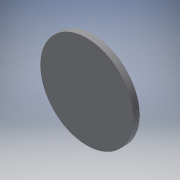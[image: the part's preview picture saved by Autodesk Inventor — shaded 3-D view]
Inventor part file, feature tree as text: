
AUTODESK INVENTOR PART (.ipt)
format: ipt  version: 2016 (Build 200138000, 138)  size: 87,552 bytes
history: native  units: in
note: dims shown in document units (in); Inventor stores cm internally (conversion verified against a paired STEP export)
features: extrude x1, sketch x1, reference x1
ambient origin geometry x8: Origin, YZ Plane, XZ Plane, XY Plane, X Axis, Y Axis, Z Axis, Center Point
bodies: Solid1 (feature_tree)
feature tree (3):
  extrude  "Extrusion1"  Depth=0.0394in TaperAngle=0.0deg
  sketch  "Sketch1"  dims[d0=0.5906in d1=0.0394in d2=0.0in]
  reference  "Reference1"
